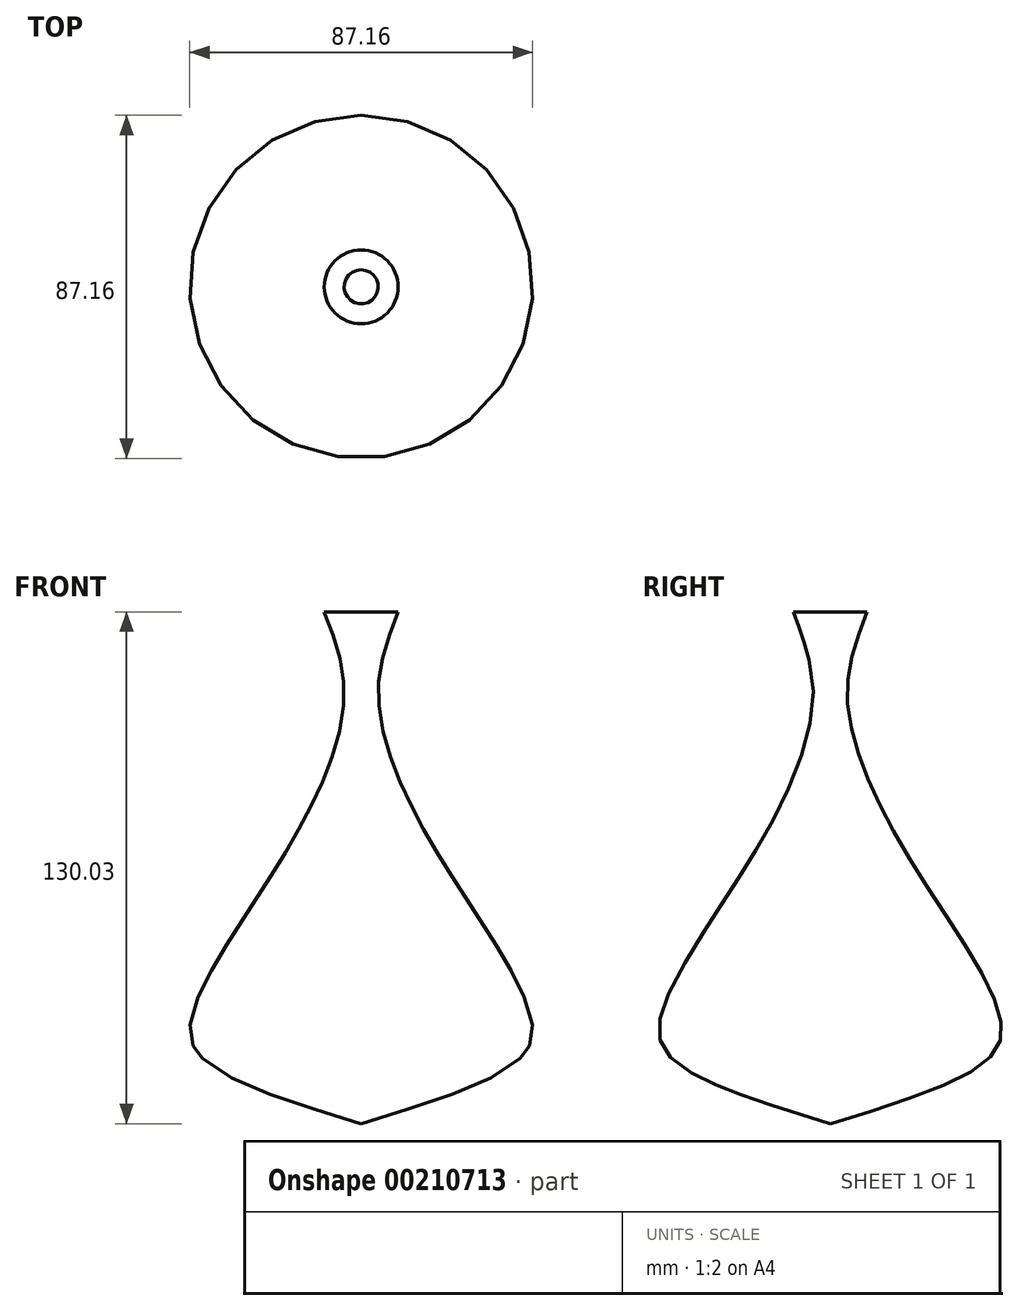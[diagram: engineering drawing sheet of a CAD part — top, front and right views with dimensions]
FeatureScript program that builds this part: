
annotation { "Feature Type Name" : "Feature", "Feature Type Description" : "" }
export const myFeature = defineFeature(function(context is Context, id is Id, definition is map)
    precondition{}
    {
        {
            var Q0;
            Q0=qCreatedBy(makeId("Right.planeOp"),FACE);
            var sketch = newSketch(context, id + "F0", { "sketchPlane" : qUnion([Q0])});
            skFitSpline(sketch, "E0", {"points": [v(9.38, 57.67) * mm, v(4.38, 38.92) * mm, v(9.06, 16.41) * mm, v(25, -12.66) * mm, v(42.82, -43.92) * mm, v(40.32, -55.8) * mm, v(0, -72.36) * mm], "startDerivative": vector(-49.1, -129) * mm, "endDerivative": vector(-238.6, -72.29) * mm});
            skLineSegment(sketch, "E1", {"start": v(0, 68.61) * mm, "end": v(0, 34.85) * mm});
            skSolve(sketch);
        }
        {
            var Q0;
            Q0=sQuery(id+"F0.wireOp",EDGE,"E0");
            var Q1;
            Q1=sQuery(id+"F0.wireOp",EDGE,"E1");
            revolve(context, id + "F1", {"bodyType" : ToolBodyType.SURFACE, "surfaceEntities" : qUnion([Q0]), "axis" : qUnion([Q1]), "revolveType" : RevolveType.FULL});
        }
    });
